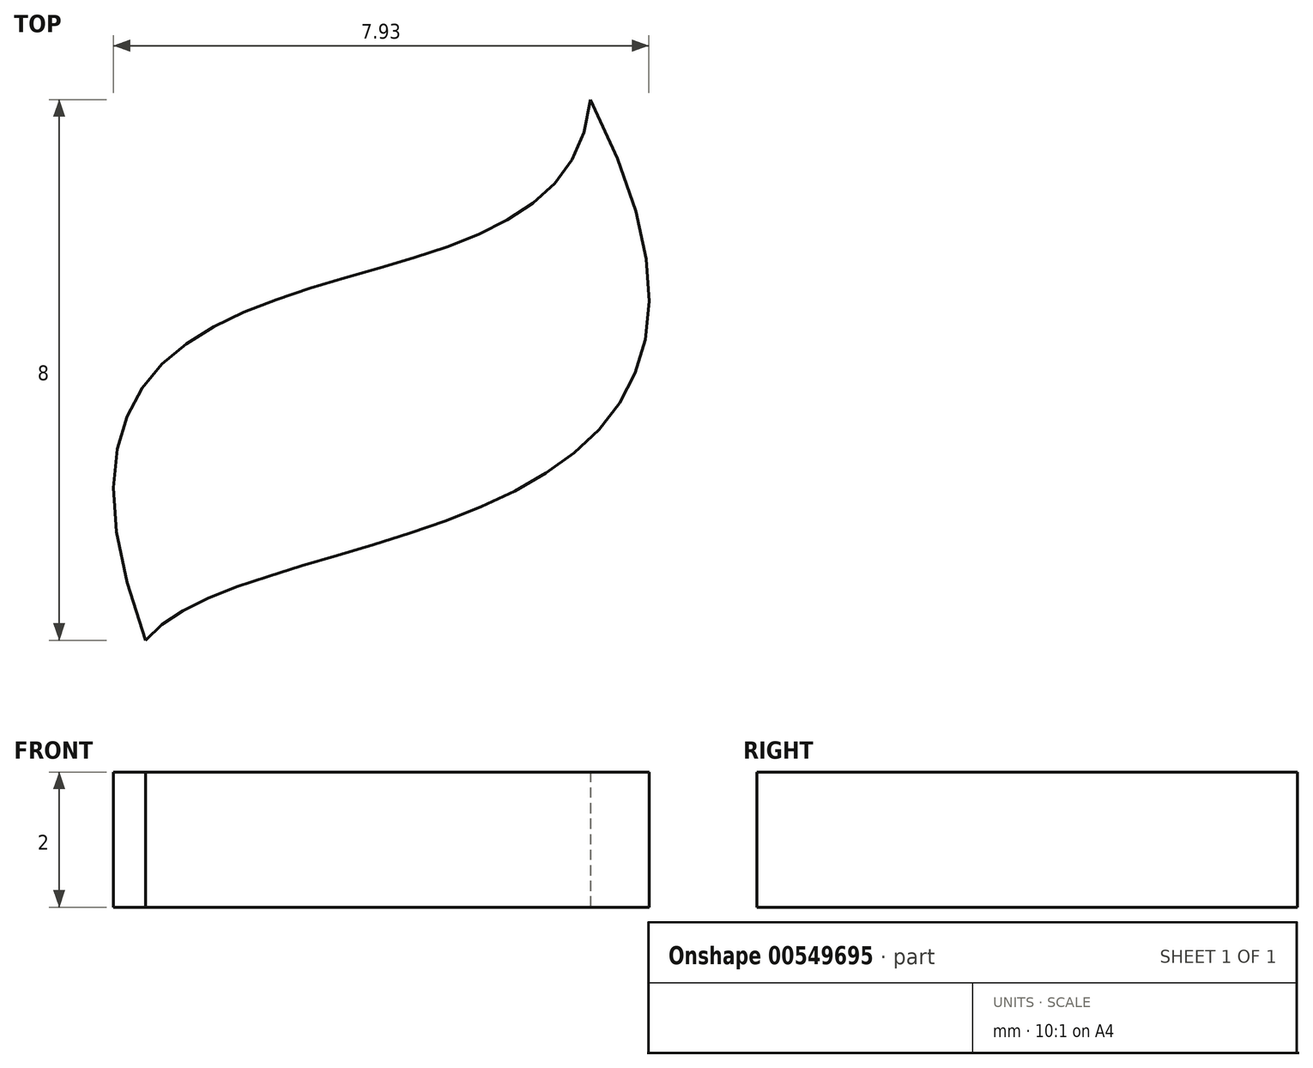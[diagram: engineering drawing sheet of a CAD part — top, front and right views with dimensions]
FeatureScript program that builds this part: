
annotation { "Feature Type Name" : "Feature", "Feature Type Description" : "" }
export const myFeature = defineFeature(function(context is Context, id is Id, definition is map)
    precondition{}
    {
        {
            var Q0;
            Q0=qCreatedBy(makeId("Top.planeOp"),FACE);
            var sketch = newSketch(context, id + "F0", { "sketchPlane" : qUnion([Q0])});
            skEllipse(sketch, "E0", {"center": v(0, 0) * mm, "majorRadius": 4.5 * mm, "minorRadius": 5 * mm, "majorAxis": v(0, -1)});
            skEllipse(sketch, "E1", {"center": v(8.7, 8.42) * mm, "majorRadius": 3 * mm, "minorRadius": 4 * mm, "majorAxis": v(0, 1)});
            skArc(sketch, "E2", {"start": v(5.72, 16.96) * mm, "mid": v(1.8, 15.22) * mm, "end": v(0.05, 11.31) * mm});
            skArc(sketch, "E3.MirrorCS", {"start": v(5.72, 16.96) * mm, "mid": v(3.96, 13.05) * mm, "end": v(0.05, 11.31) * mm});
            skArc(sketch, "E4", {"start": v(-5.6, 16.98) * mm, "mid": v(-3.85, 13.07) * mm, "end": v(0.05, 11.31) * mm});
            skPoint(sketch, "E5.0.internal.snap0", {"position": v(0, -4.5) * mm});
            skFitSpline(sketch, "E6", {"points": [v(-14.05, 3.8) * mm, v(-7.46, 11.8) * mm], "startDerivative": vector(-7.75, 20.91) * mm, "endDerivative": vector(1.12, 11.88) * mm});
            skFitSpline(sketch, "E7", {"points": [v(-7.46, 11.8) * mm, v(-14.05, 3.8) * mm], "startDerivative": vector(10.78, -20.91) * mm, "endDerivative": vector(-4.64, -5.64) * mm});
            skArc(sketch, "E8.MirrorCS", {"start": v(-5.6, 16.98) * mm, "mid": v(-1.69, 15.22) * mm, "end": v(0.05, 11.31) * mm});
            skLineSegment(sketch, "E9", {"start": v(-5.6, 16.98) * mm, "end": v(0.05, 11.31) * mm});
            skLineSegment(sketch, "E10", {"start": v(0.05, 11.31) * mm, "end": v(5.72, 16.96) * mm});
            skLineSegment(sketch, "E11", {"start": v(0, 4.5) * mm, "end": v(0, -4.5) * mm});
            skLineSegment(sketch, "E12", {"start": v(8.7, 11.42) * mm, "end": v(8.7, 5.42) * mm});
            skSolve(sketch);
        }
        {
            var Q0;
            Q0=makeQuery(id+"F0.imprint","IMPRINT",FACE,{"disambiguationData":[TD([[makeQuery(id+"F0.imprint","IMPRINT",EDGE,{"derivedFrom":sQuery(id+"F0.wireOp",EDGE,"E6")}),-1.0]])]});
            extrude(context, id + "F1", {"entities" : qUnion([Q0]), "depth" : 2 * mm, "offsetDistance" : 25 * mm});
        }
    });
